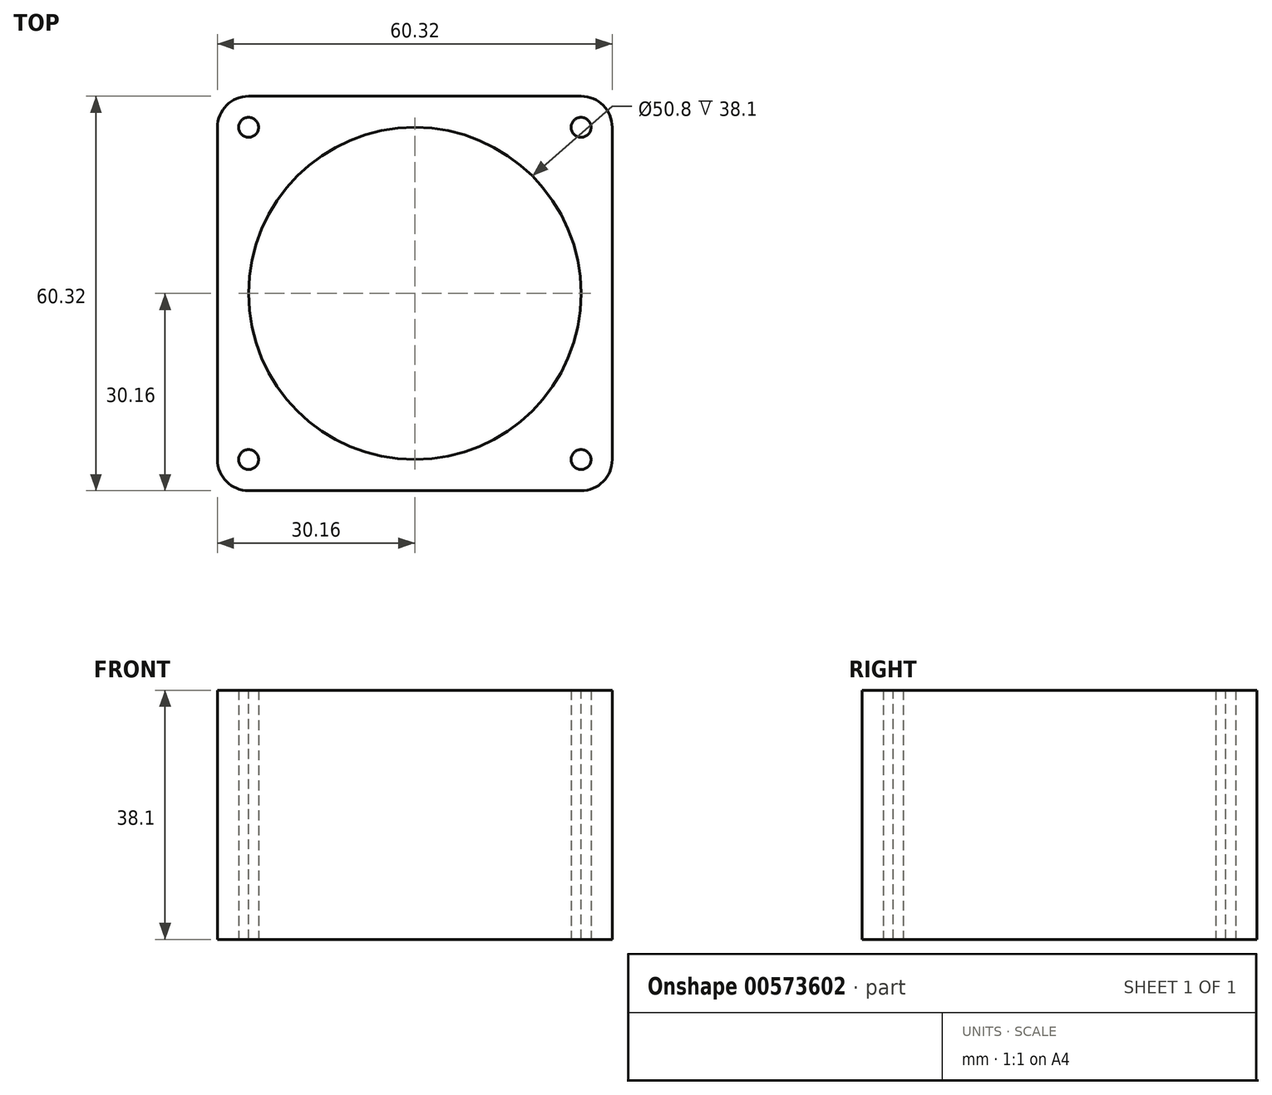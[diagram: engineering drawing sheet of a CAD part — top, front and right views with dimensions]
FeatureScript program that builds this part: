
annotation { "Feature Type Name" : "Feature", "Feature Type Description" : "" }
export const myFeature = defineFeature(function(context is Context, id is Id, definition is map)
    precondition{}
    {
        {
            var Q0;
            Q0=qCreatedBy(makeId("Top.planeOp"),FACE);
            var sketch = newSketch(context, id + "F0", { "sketchPlane" : qUnion([Q0])});
            skLineSegment(sketch, "E0.bottom", {"start": v(25.4, 30.16) * mm, "end": v(-25.4, 30.16) * mm});
            skLineSegment(sketch, "E0.top", {"start": v(25.4, -30.16) * mm, "end": v(-25.4, -30.16) * mm});
            skLineSegment(sketch, "E0.left", {"start": v(30.16, 25.4) * mm, "end": v(30.16, -25.4) * mm});
            skLineSegment(sketch, "E0.right", {"start": v(-30.16, 25.4) * mm, "end": v(-30.16, -25.4) * mm});
            skPoint(sketch, "E0.middle", {"position": v(0, 0) * mm});
            skPoint(sketch, "E1.visualSharp", {"position": v(-30.16, 30.16) * mm});
            skArc(sketch, "E1.filletArc", {"start": v(-25.4, 30.16) * mm, "mid": v(-28.77, 28.77) * mm, "end": v(-30.16, 25.4) * mm});
            skPoint(sketch, "E2.visualSharp", {"position": v(30.16, 30.16) * mm});
            skArc(sketch, "E2.filletArc", {"start": v(30.16, 25.4) * mm, "mid": v(28.77, 28.77) * mm, "end": v(25.4, 30.16) * mm});
            skPoint(sketch, "E3.visualSharp", {"position": v(30.16, -30.16) * mm});
            skArc(sketch, "E3.filletArc", {"start": v(25.4, -30.16) * mm, "mid": v(28.77, -28.77) * mm, "end": v(30.16, -25.4) * mm});
            skPoint(sketch, "E4.visualSharp", {"position": v(-30.16, -30.16) * mm});
            skArc(sketch, "E4.filletArc", {"start": v(-30.16, -25.4) * mm, "mid": v(-28.77, -28.77) * mm, "end": v(-25.4, -30.16) * mm});
            skCircle(sketch, "E5", {"center": v(-25.4, 25.4) * mm, "radius": 1.52 * mm});
            skCircle(sketch, "E6", {"center": v(25.4, 25.4) * mm, "radius": 1.52 * mm});
            skCircle(sketch, "E7", {"center": v(-25.4, -25.4) * mm, "radius": 1.52 * mm});
            skCircle(sketch, "E8", {"center": v(25.4, -25.4) * mm, "radius": 1.52 * mm});
            skSolve(sketch);
        }
        {
            var Q0;
            Q0 = qSketchRegion(id + "F0", true);
            extrude(context, id + "F1", {"entities" : qUnion([Q0]), "depth" : 38.1 * mm, "offsetDistance" : 25.4 * mm});
        }
        {
            var Q0;
            Q0=makeQuery(id+"F1.opExtrude","CAP_FACE",FACE,{"disambiguationData":[OSD([sQuery(id+"F0.wireOp",EDGE,"E0.bottom"),sQuery(id+"F0.wireOp",EDGE,"E0.top"),sQuery(id+"F0.wireOp",EDGE,"E0.left"),sQuery(id+"F0.wireOp",EDGE,"E0.right"),sQuery(id+"F0.wireOp",EDGE,"E1.filletArc"),sQuery(id+"F0.wireOp",EDGE,"E2.filletArc"),sQuery(id+"F0.wireOp",EDGE,"E3.filletArc"),sQuery(id+"F0.wireOp",EDGE,"E4.filletArc"),sQuery(id+"F0.wireOp",EDGE,"E5"),sQuery(id+"F0.wireOp",EDGE,"E6"),sQuery(id+"F0.wireOp",EDGE,"E7"),sQuery(id+"F0.wireOp",EDGE,"E8")])],"isStart":false});
            var sketch = newSketch(context, id + "F2", { "sketchPlane" : qUnion([Q0])});
            skCircle(sketch, "E9", {"center": v(0, 0) * mm, "radius": 25.4 * mm});
            skSolve(sketch);
        }
        {
            var Q0;
            Q0=makeQuery(id+"F2.imprint","IMPRINT",FACE,{"disambiguationData":[TD([[makeQuery(id+"F2.imprint","IMPRINT",EDGE,{"derivedFrom":sQuery(id+"F2.wireOp",EDGE,"E9")}),1.0]])]});
            extrude(context, id + "F3", {"entities" : qUnion([Q0]), "operationType" : NewBodyOperationType.REMOVE, "endBound" : BoundingType.THROUGH_ALL, "oppositeDirection" : true, "depth" : 25.4 * mm, "offsetDistance" : 25.4 * mm});
        }
    });
